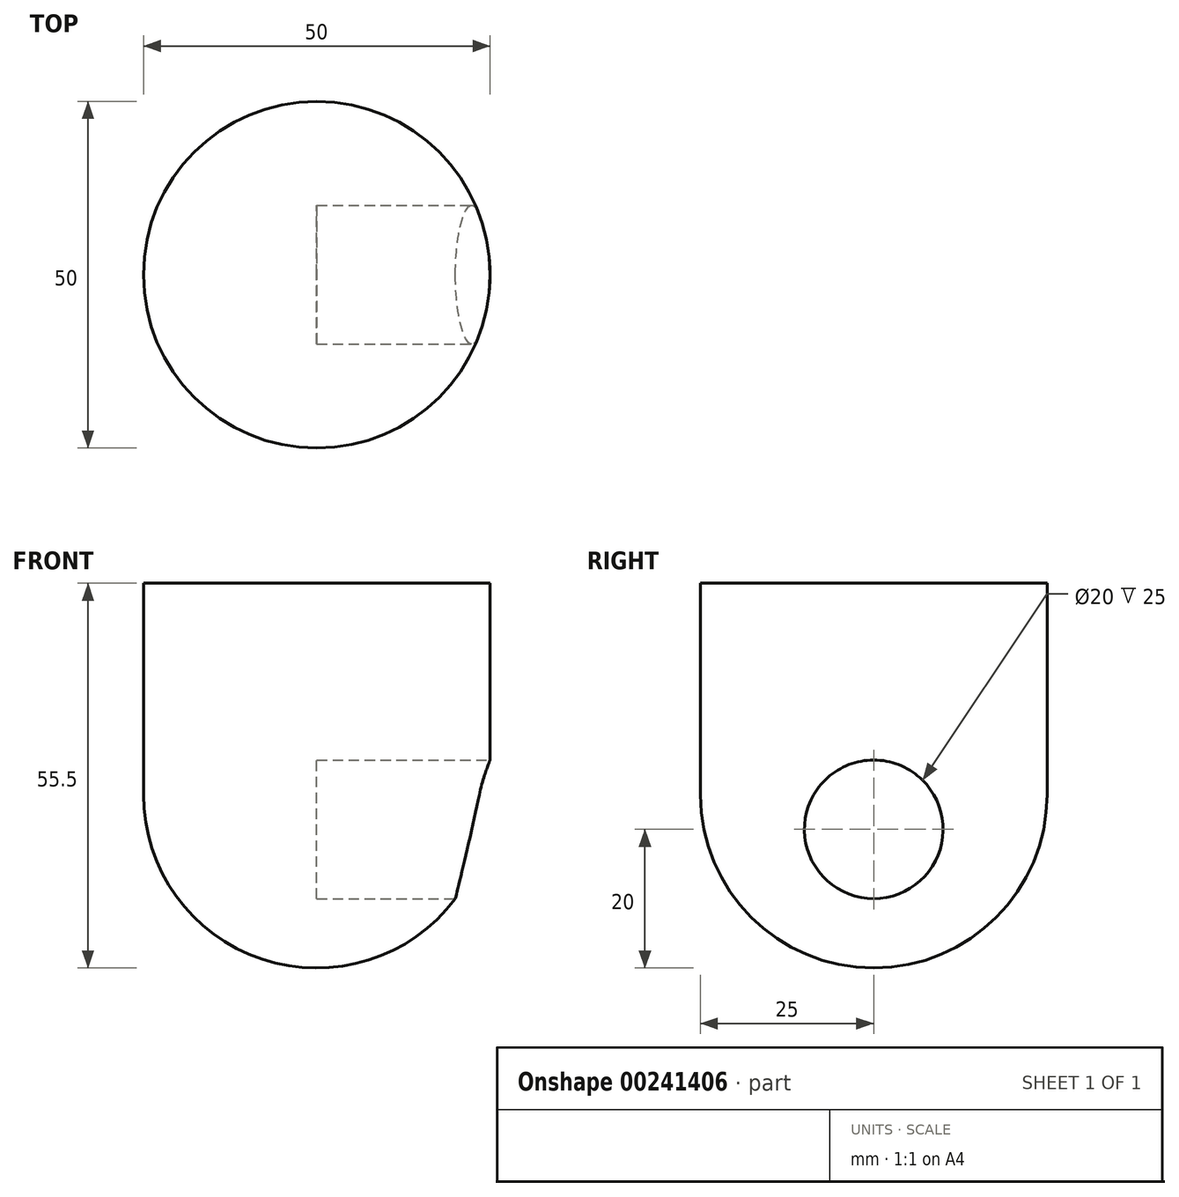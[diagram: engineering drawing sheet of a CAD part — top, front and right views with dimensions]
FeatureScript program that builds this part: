
annotation { "Feature Type Name" : "Feature", "Feature Type Description" : "" }
export const myFeature = defineFeature(function(context is Context, id is Id, definition is map)
    precondition{}
    {
        {
            var Q0;
            Q0=qCreatedBy(makeId("Top.planeOp"),FACE);
            var sketch = newSketch(context, id + "F0", { "sketchPlane" : qUnion([Q0])});
            skLineSegment(sketch, "E0.bottom", {"start": v(-25, 25) * mm, "end": v(25, 25) * mm});
            skLineSegment(sketch, "E0.top", {"start": v(-25, -25) * mm, "end": v(25, -25) * mm});
            skLineSegment(sketch, "E0.left", {"start": v(-25, 25) * mm, "end": v(-25, -25) * mm});
            skLineSegment(sketch, "E0.right", {"start": v(25, 25) * mm, "end": v(25, -25) * mm});
            skPoint(sketch, "E0.middle", {"position": v(0, 0) * mm});
            skSolve(sketch);
        }
        {
            var Q0;
            Q0 = qSketchRegion(id + "F0", true);
            extrude(context, id + "F1", {"entities" : qUnion([Q0]), "depth" : 55.5 * mm});
        }
        {
            var Q0;
            Q0=makeQuery(id+"F1.opExtrude","SWEPT_FACE",FACE,{"disambiguationData":[OSD([sQuery(id+"F0.wireOp",EDGE,"E0.right")])]});
            var sketch = newSketch(context, id + "F2", { "sketchPlane" : qUnion([Q0])});
            skCircle(sketch, "E1", {"center": v(0, 20) * mm, "radius": 10 * mm});
            skSolve(sketch);
        }
        {
            var Q0;
            Q0 = qSketchRegion(id + "F2", true);
            extrude(context, id + "F3", {"entities" : qUnion([Q0]), "operationType" : NewBodyOperationType.REMOVE, "oppositeDirection" : true, "depth" : 25 * mm});
        }
        {
            var Q0;
            Q0=makeQuery(id+"F1.opExtrude","CAP_EDGE",EDGE,{"disambiguationData":[OSD([sQuery(id+"F0.wireOp",EDGE,"E0.top")])],"isStart":true});
            var Q1;
            Q1=makeQuery(id+"F1.opExtrude","CAP_EDGE",EDGE,{"disambiguationData":[OSD([sQuery(id+"F0.wireOp",EDGE,"E0.bottom")])],"isStart":true});
            fillet(context, id + "F4", {"entities" : qUnion([Q0, Q1]), "radius" : 25 * mm, "tangentPropagation" : true, "allowEdgeOverflow" : false});
        }
        {
            var Q0;
            Q0=makeQuery(id+"F1.opExtrude","SWEPT_EDGE",EDGE,{"disambiguationData":[OSD([sQuery(id+"F0.wireOp",EDGE,"E0.top"),sQuery(id+"F0.wireOp",EDGE,"E0.right")])]});
            var Q1;
            Q1=makeQuery(id+"F1.opExtrude","SWEPT_EDGE",EDGE,{"disambiguationData":[OSD([sQuery(id+"F0.wireOp",EDGE,"E0.top"),sQuery(id+"F0.wireOp",EDGE,"E0.left")])]});
            fillet(context, id + "F5", {"entities" : qUnion([Q0, Q1]), "radius" : 25 * mm, "tangentPropagation" : true, "allowEdgeOverflow" : false});
        }
    });
